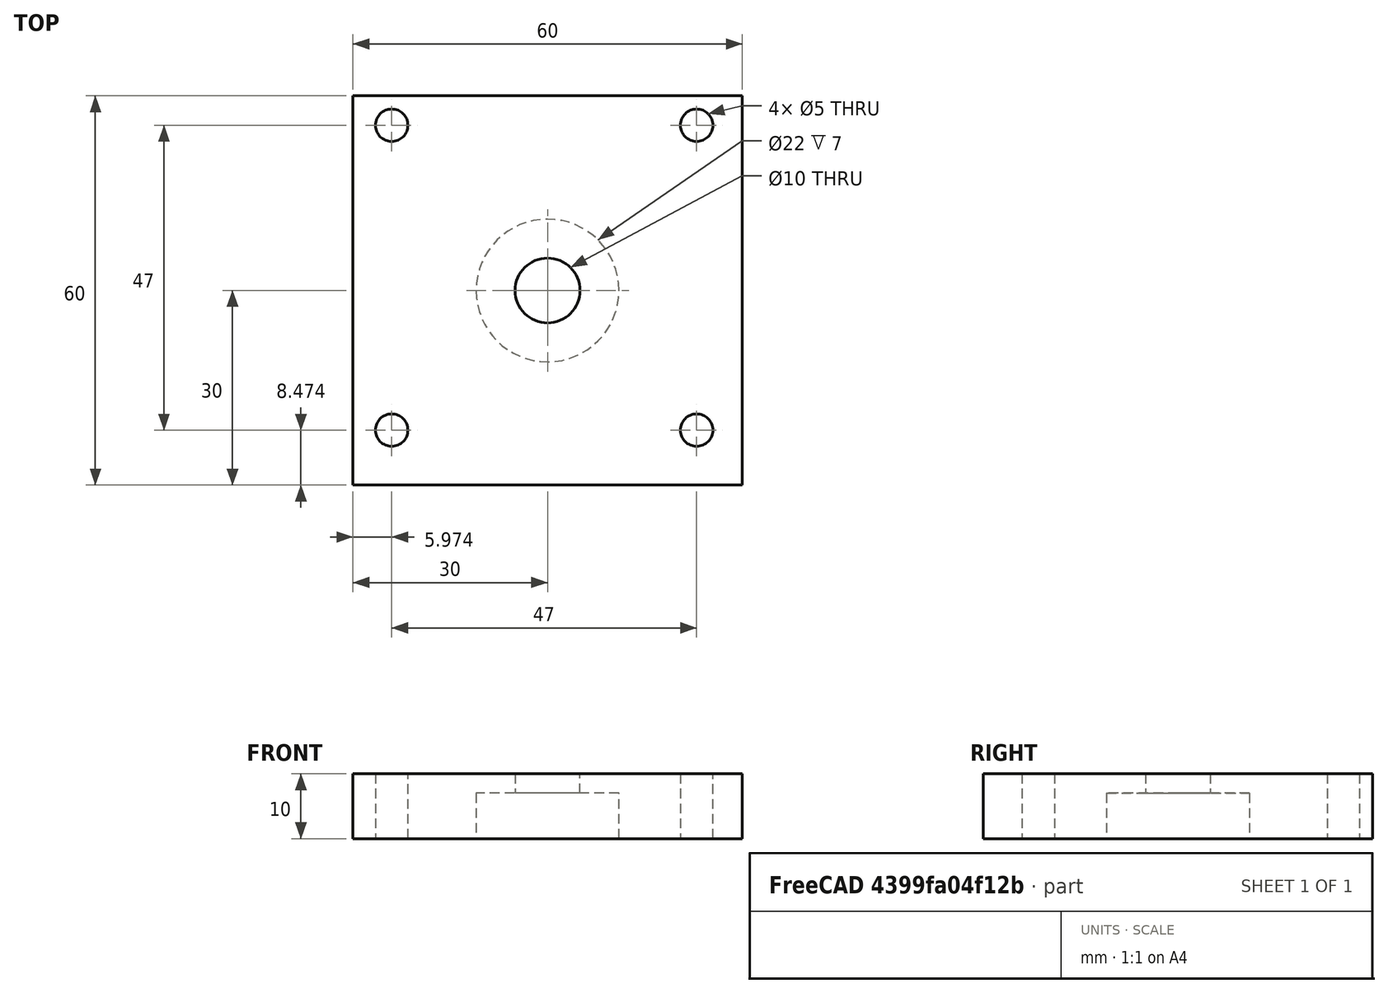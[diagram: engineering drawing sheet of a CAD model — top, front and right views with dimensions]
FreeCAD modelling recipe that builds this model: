
FCSTD DOCUMENT  (FreeCAD 1.0R38641 +678 (Git))
Label: Bearing-Holder
License: All rights reserved
LicenseURL: https://en.wikipedia.org/wiki/All_rights_reserved
objects: Sketcher::SketchObject×4, PartDesign::Pocket×3, Mesh::Feature×1, PartDesign::Pad×1, PartDesign::Body×1
note: 21 computed .brp shape members not serialized (recipe doc carries the construction recipe); baked Part::Feature solids carry a one-line shape summary decoded from their .brp

FEATURE [Mesh::Feature] nema23_base_plate_v2_1_  label="nema23_base_plate_v2(1)"
FEATURE [Sketcher::SketchObject] Sketch
  ArcFitTolerance = 1e-06
  AttachmentSupport = -> [XY_Plane]
  FullyConstrained = true
  MakeInternals = false
  MapMode = 5
  sketch-geometry (5):
    g0: LineSegment StartX=-30 StartY=-30 StartZ=0 EndX=30 EndY=-30 EndZ=0
    g1: LineSegment StartX=30 StartY=-30 StartZ=0 EndX=30 EndY=30 EndZ=0
    g2: LineSegment StartX=30 StartY=30 StartZ=0 EndX=-30 EndY=30 EndZ=0
    g3: LineSegment StartX=-30 StartY=30 StartZ=0 EndX=-30 EndY=-30 EndZ=0
    g4: GeomPoint [constr] X=0 Y=0 Z=0
  constraints (12):
    c: Coincident(g0,g1)
    c: Coincident(g1,g2)
    c: Coincident(g2,g3)
    c: Coincident(g3,g0)
    c: Horizontal(g0)
    c: Horizontal(g2)
    c: Vertical(g1)
    c: Vertical(g3)
    c: Symmetric(g2,g0,g4)
    c: Distance(g1,g3) = 60
    c: Distance(g0,g2) = 60
    c: Coincident(g4,g-1)
FEATURE [PartDesign::Pad] Pad
  Direction = (0,0,1)
  Length = 10
  Length2 = 10
  Profile = -> Sketch
  ReferenceAxis = -> Sketch [N_Axis]
  Refine = true
  Suppressed = false
  Type = 0
FEATURE [Sketcher::SketchObject] Sketch001
  ArcFitTolerance = 1e-06
  AttachmentSupport = -> [Pad]
  FullyConstrained = false
  MakeInternals = false
  MapMode = 5
  Placement = pos=(0,0,0) rot=(1,0,0;3.14159rad)
  sketch-geometry (4):
    g0: Circle CenterX=22.974 CenterY=-25.4744 CenterZ=0 NormalX=0 NormalY=0 NormalZ=1 AngleXU=0 Radius=2.5
    g1: Circle CenterX=-24.026 CenterY=-25.4744 CenterZ=0 NormalX=0 NormalY=0 NormalZ=1 AngleXU=0 Radius=2.5
    g2: Circle CenterX=-24.026 CenterY=21.5256 CenterZ=0 NormalX=0 NormalY=0 NormalZ=1 AngleXU=0 Radius=2.5
    g3: Circle CenterX=22.974 CenterY=21.5256 CenterZ=0 NormalX=0 NormalY=0 NormalZ=1 AngleXU=0 Radius=2.5
  constraints (10):
    c: Diameter(g0) = 5
    c: Diameter(g1) = 5
    c: Diameter(g2) = 5
    c: Diameter(g3) = 5
    c: Vertical(g3,g0)
    c: Vertical(g2,g1)
    c: Horizontal(g3,g2)
    c: Horizontal(g1,g0)
    c: Distance(g3,g0) = 42
    c: Distance(g1,g0) = 42
FEATURE [PartDesign::Pocket] Pocket
  BaseFeature = -> Pad
  Direction = (0,0,1)
  Length = 10
  Length2 = 5
  Profile = -> Sketch001
  ReferenceAxis = -> Sketch001 [N_Axis]
  Refine = true
  Suppressed = false
  Type = 0
FEATURE [Sketcher::SketchObject] Sketch002
  ArcFitTolerance = 1e-06
  AttachmentSupport = -> [Pocket]
  FullyConstrained = true
  MakeInternals = false
  MapMode = 5
  Placement = pos=(0,0,0) rot=(1,0,0;3.14159rad)
  sketch-geometry (1):
    g0: Circle CenterX=0 CenterY=0 CenterZ=0 NormalX=0 NormalY=0 NormalZ=1 AngleXU=0 Radius=11
  constraints (2):
    c: Diameter(g0) = 22
    c: Coincident(g0,g-1)
FEATURE [PartDesign::Pocket] Pocket001
  BaseFeature = -> Pocket
  Direction = (0,0,1)
  Length = 7
  Length2 = 5
  Profile = -> Sketch002
  ReferenceAxis = -> Sketch002 [N_Axis]
  Refine = true
  Suppressed = false
  Type = 0
FEATURE [Sketcher::SketchObject] Sketch003
  ArcFitTolerance = 1e-06
  AttachmentSupport = -> [Pocket001]
  FullyConstrained = true
  MakeInternals = false
  MapMode = 5
  Placement = pos=(0,0,7) rot=(1,0,0;3.14159rad)
  sketch-geometry (1):
    g0: Circle CenterX=0 CenterY=0 CenterZ=0 NormalX=0 NormalY=0 NormalZ=1 AngleXU=0 Radius=5
  constraints (2):
    c: Diameter(g0) = 10
    c: Coincident(g0,g-1)
FEATURE [PartDesign::Pocket] Pocket002
  BaseFeature = -> Pocket001
  Direction = (0,0,1)
  Length = 5
  Length2 = 5
  Profile = -> Sketch003
  ReferenceAxis = -> Sketch003 [N_Axis]
  Refine = true
  Suppressed = false
  Type = 0
FEATURE [PartDesign::Body] Body
  AllowCompound = false
  Group = -> [Sketch,Pad,Sketch001,Pocket,Sketch002,Pocket001,Sketch003,Pocket002]
  Origin = -> Origin
  Placement = pos=(0.4,0.8,-12) rot=(0,0,1;0rad)
  Tip = -> Pocket002
